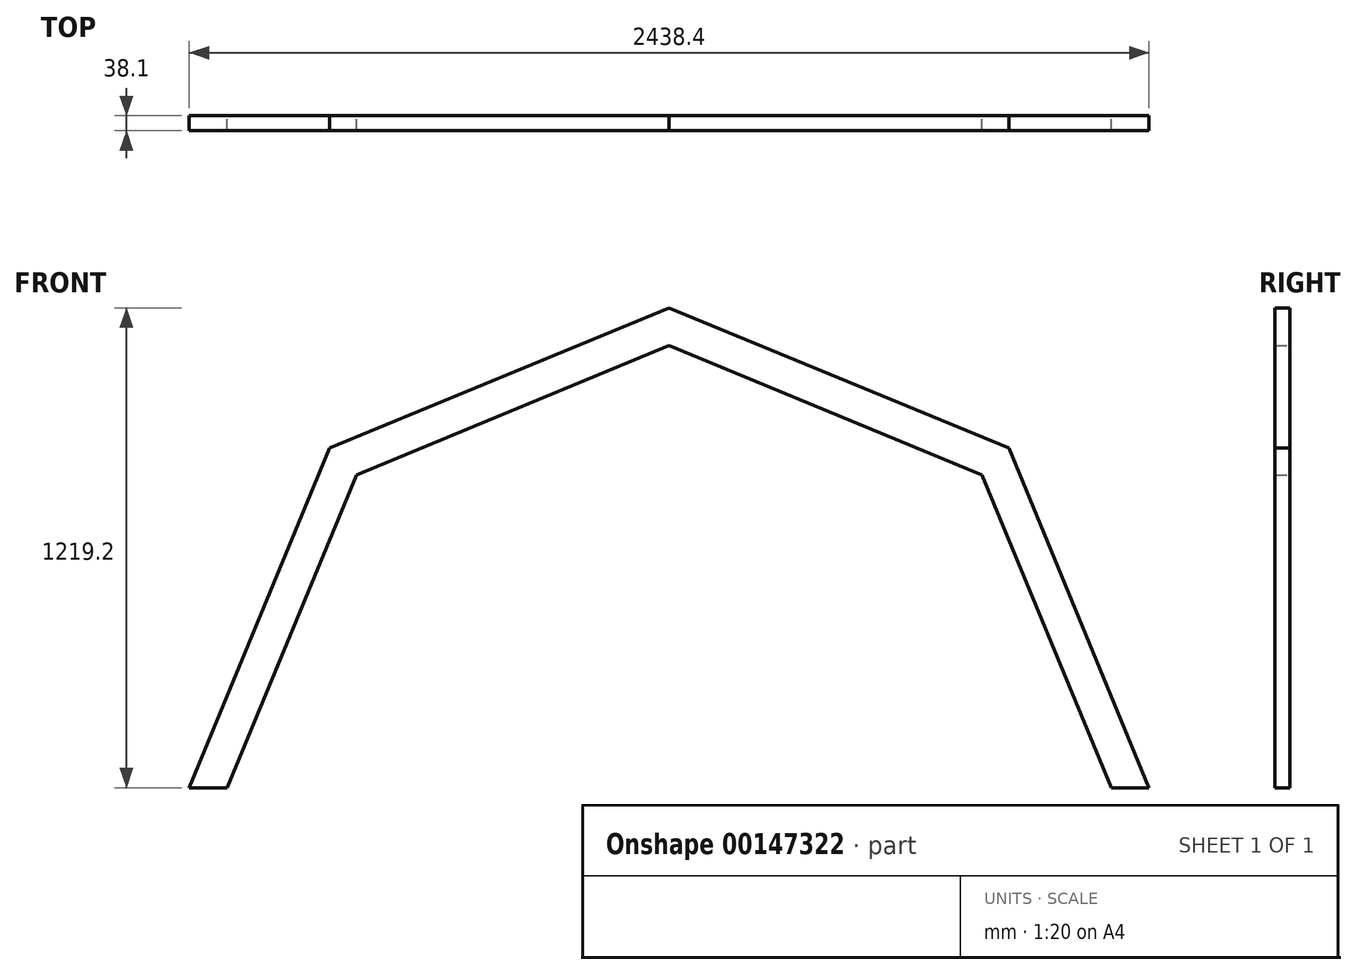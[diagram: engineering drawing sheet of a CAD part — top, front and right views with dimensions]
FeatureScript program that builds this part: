
annotation { "Feature Type Name" : "Feature", "Feature Type Description" : "" }
export const myFeature = defineFeature(function(context is Context, id is Id, definition is map)
    precondition{}
    {
        {
            var Q0;
            Q0=qCreatedBy(makeId("Front.planeOp"),FACE);
            var sketch = newSketch(context, id + "F0", { "sketchPlane" : qUnion([Q0])});
            skLineSegment(sketch, "E0.top", {"start": v(-1027.18, -196.14) * mm, "end": v(-930.98, -196.14) * mm});
            skLineSegment(sketch, "E1", {"start": v(-1027.18, -196.14) * mm, "end": v(-670.66, 666.55) * mm});
            skLineSegment(sketch, "E2", {"start": v(-670.66, 666.55) * mm, "end": v(192.02, 1023.06) * mm});
            skLineSegment(sketch, "E3", {"start": v(-930.98, -196.14) * mm, "end": v(-602.6, 598.48) * mm});
            skLineSegment(sketch, "E4", {"start": v(-602.6, 598.48) * mm, "end": v(192.02, 926.87) * mm});
            skLineSegment(sketch, "E5.top", {"start": v(1315.03, -196.14) * mm, "end": v(1411.22, -196.14) * mm});
            skLineSegment(sketch, "E6.MirrorCS", {"start": v(1315.03, -196.14) * mm, "end": v(986.64, 598.48) * mm});
            skLineSegment(sketch, "E7.MirrorCS", {"start": v(1411.22, -196.14) * mm, "end": v(1054.7, 666.55) * mm});
            skLineSegment(sketch, "E8.MirrorCS", {"start": v(986.64, 598.48) * mm, "end": v(192.02, 926.87) * mm});
            skLineSegment(sketch, "E9.MirrorCS", {"start": v(1054.7, 666.55) * mm, "end": v(192.02, 1023.06) * mm});
            skSolve(sketch);
        }
        {
            var Q0;
            Q0=qSketchRegion(id+"F0",true);
            extrude(context, id + "F1", {"entities" : qUnion([Q0]), "endBound" : BoundingType.SYMMETRIC, "depth" : 38.1 * mm});
        }
    });
